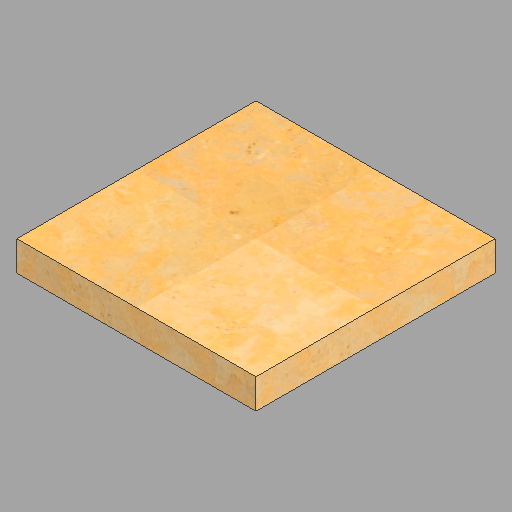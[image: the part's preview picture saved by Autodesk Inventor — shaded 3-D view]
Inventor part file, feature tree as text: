
AUTODESK INVENTOR PART (.ipt)
format: ipt  version: 2023 (Build 270158030, 158C)  size: 265,216 bytes
history: native  units: in
note: dims shown in document units (in); Inventor stores cm internally (conversion verified against a paired STEP export)
features: other x1, extrude x1, sketch x1
ambient origin geometry x8: Origin, YZ Plane, XZ Plane, XY Plane, X Axis, Y Axis, Z Axis, Center Point
bodies: Solid1 (feature_tree)
feature tree (3):
  other  "16x16x2 - 53"
  extrude  "Extrusion1"  Depth=16.0in
  sketch  "Sketch1"  dims[d0=16.0in d1=16.0in d2=2.0in d3=0.0in]
